# Revit family: Pump_Commercial-Effluent-Zoeller-140_145_Series
name_source: partatom
category: Mechanical Equipment
revit_build: Autodesk Revit 2014 (Build: 20130308_1515(x64)
units: mm (PartAtom-declared; Revit-internal decimal feet)

## types (4) — shared parameters
Apparent Load = 1380 VA
Assembly Code = D2010900
Cooling = Oil filled
Cord Length = 240"
Cord Type = UL listed, neoprene.
Default Elevation = 0"
Description = Effluent or dewatering submersible pump for septic tank, low pressure pipe (LPP) and enhanced flow STEP systems.
Discharge Diameter = 1 1/2" NPT
Discharge Height = 4 5/32"
Discharge Radius = 3/4"
Height = 12 13/32"
Hertz = 60
Impeller = Engineered Thermoplastic
Installation Type = Floor Mounted
Insulation = Class B
Lead Wires Insulation = Class B
Length = 7 13/16"
Manufacturer = Zoeller
Material = Cast Iron-Zoeller-Powder Coated Epoxy
Max. Water Temp. = 130 °F
Motor Thermal Shutoff = Auto Reset Thermal Overload.
Motor Type = Submersible
O-Rings and Cover Gasket = Neoprene
Operation = Automatic or Nonautomatic
Phase = 1
Price = Prices may vary. Please consult Manufacturer Representative for most up-to-date price list.
Product Page URL = http://www.zoellerpumps.com
RPM = 3450 RPM
Shaft Seal = Carbon and Ceramic
Type = Permanent Split Capacitor
URL = http://www.zoellerpumps.com
Warranty Information = 18 Months (Limited)
Waste Connection = Yes
Width = 10 3/16"

## per-type parameters (varying)
| type | Amps | Impeller Type | Max Flow @ 5' | Maximum Head | Model | Motor | Solid Handling | Voltage |
| 140 - 115V 1Ph | 12 A | Non-clogging vortex | 86 GPM | 600" | 140 | 1 HP | 1/2" Spherical Solids | 115 V |
| 145 - 115V 1Ph | 12 A | Single vane | 61 GPM | 888" | 145 | 3/4 HP | 3/4" Spherical Solids | 115 V |
| 140 - 230V 1Ph | 6 A | Non-clogging vortex | 86 GPM | 600" | 140 | 1 HP | 1/2" Spherical Solids | 230 V |
| 145 - 230V 1Ph | 6 A | Single vane | 61 GPM | 888" | 145 | 3/4 HP | 3/4" Spherical Solids | 230 V |

## geometry (parser evidence)
native form markers: Sweep x1
no freeform markers — native parametric forms only
